# Revit family: PRD_FrankeWS_WCPnCnnctrs_CampusCommunicationPreventer_ZCMPX0001
name_source: partatom
category: Pipe Fittings
revit_build: Autodesk Revit 2018 (Build: 20190510_1515(x64)
units: mm (PartAtom-declared; Revit-internal decimal feet)

## family parameters
Always vertical = No
Cut with Voids When Loaded = No
OmniClass Number = 23.60.30.11.14
OmniClass Title = Pipework Fittings
Part Type = Union
Round Connector Dimension = Use Diameter
Shared = No
Work Plane-Based = No

## types (1)
- ZCMPX0001
    AssetType = Fixed
    BIMObjectName = PRD_AR_WCPanConnectors_CampusCommunicationPreventer_ZCMPX0001
    Category = Pr_40_20_93_93, WC pan connectors
    CommunicationPreventerMaterial = PRD_AR_PE
    Description = Communication preventer for the use in prisons to prevent communication between prison cells using the WC pipework, for connection to WC flushing pipes DN100, material PE (weldable), EN 997 approved, EN 476 approved, DIN 1389 approved.
    DurationUnit = year
    Features = Communication preventer, 140x140x180 mm (WxHxD)
    FittingLossFactor = 0
    GrossWeight = 0.52 kg
    IfcExportAs = IfcPipeFittingType
    IfcExportType = NOTDEFINED
    InnerDiameter = 102
    Jointing = Push fit
    Manufacturer = KWC Group AG
    ManufacturerName = KWC Group AG
    ManufacturerURL = www.kwc.com
    Material = PE (weldable)
    Model = ZCMPX0001
    ModelNumber = 2000102705
    ModelReference = ZCMPX0001
    NBSDescription = WC pan connectors
    NBSReference = 45-35-70/390
    Name = CAMPUS communication preventer ZCMPX0001
    NetWeight = 0.47 kg
    NominalDiameter = 100 mm  [stored 0.328084 ft]
    NominalHeight = 140 mm  [stored 0.459318 ft]
    NominalLength = 180 mm  [stored 0.590551 ft]
    NominalWidth = 140 mm  [stored 0.459318 ft]
    OuterDiameter = 110
    PressureClass = 0.0 Pa
    ProductInformation = https://pim.kwc.com
    Shape = Cylindrical
    Size = DN 100
    Standard = EN 997, EN 476, DIN 1389
    SubType = OTHER
    URL = www.kwc.com
    Uniclass2015Code = Pr_40_20_93_93
    Uniclass2015Title = WC pan connectors
    Uniclass2015Version = Products v1.5
    UnitWeight = 0.52 kg
    Version = 1
    WarrantyDurationUnit = year

note: [stored X ft] marks values corroborated as IEEE doubles in the binary element streams (Revit-internal decimal feet)

## geometry (parser evidence)
native form markers: Sweep x2
no freeform markers — native parametric forms only
